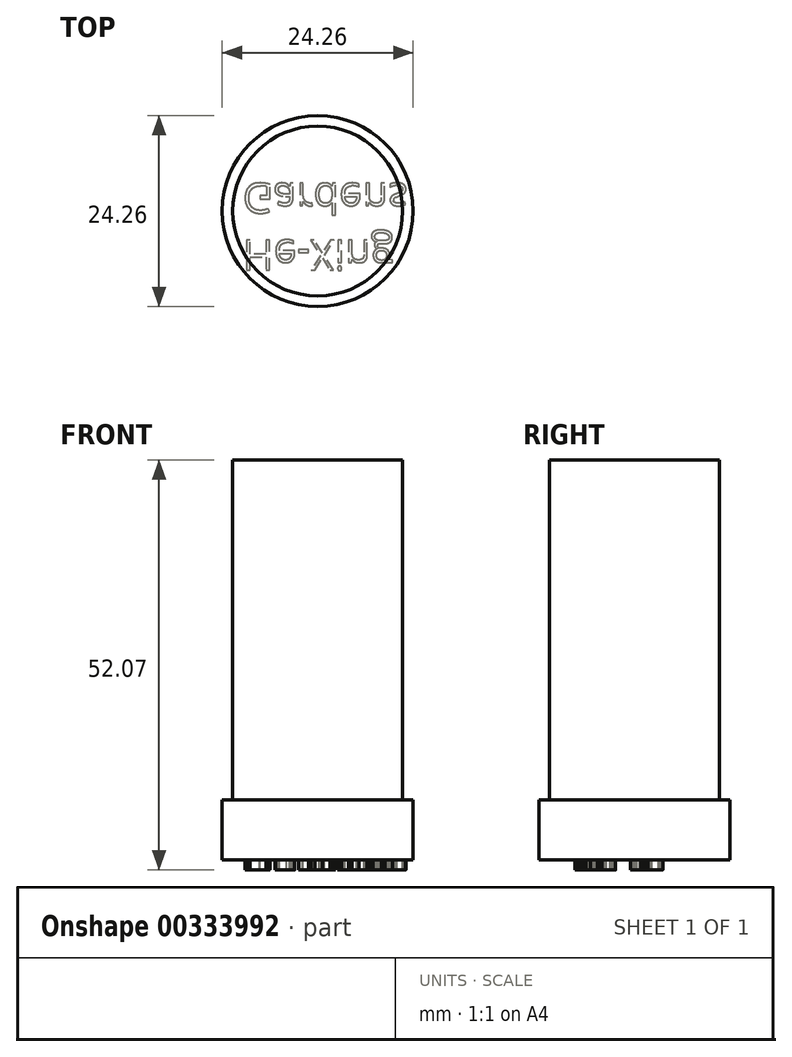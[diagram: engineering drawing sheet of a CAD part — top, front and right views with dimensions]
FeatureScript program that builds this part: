
annotation { "Feature Type Name" : "Feature", "Feature Type Description" : "" }
export const myFeature = defineFeature(function(context is Context, id is Id, definition is map)
    precondition{}
    {
        {
            var Q0;
            Q0=qCreatedBy(makeId("Top.planeOp"),FACE);
            var sketch = newSketch(context, id + "F0", { "sketchPlane" : qUnion([Q0])});
            skCircle(sketch, "E0", {"center": v(0, 0) * mm, "radius": 12.13 * mm});
            skCircle(sketch, "E1", {"center": v(0, 0) * mm, "radius": 10.8 * mm});
            skSolve(sketch);
        }
        {
            var Q0;
            Q0=makeQuery(id+"F0.imprint","IMPRINT",FACE,{"disambiguationData":[TD([[makeQuery(id+"F0.imprint","IMPRINT",EDGE,{"derivedFrom":sQuery(id+"F0.wireOp",EDGE,"E1")}),1.0]])]});
            extrude(context, id + "F1", {"entities" : qUnion([Q0]), "depth" : 50.8 * mm});
        }
        {
            var Q0;
            Q0 = qSketchRegion(id + "F0", true);
            extrude(context, id + "F2", {"entities" : qUnion([Q0]), "operationType" : NewBodyOperationType.ADD, "depth" : 7.62 * mm});
        }
        {
            var Q0;
            {var subQ0=sQuery(id+"F0.wireOp",EDGE,"E1");Q0=makeQuery(id+"F2.boolean.opBoolean","MERGE",FACE,{"derivedFrom":[makeQuery(id+"F1.opExtrude","CAP_FACE",FACE,{"disambiguationData":[OSD([subQ0])],"isStart":true}),makeQuery(id+"F2.opExtrude","CAP_FACE",FACE,{"disambiguationData":[OSD([sQuery(id+"F0.wireOp",EDGE,"E0"),subQ0])],"isStart":true})]});}
            var sketch = newSketch(context, id + "F3", { "sketchPlane" : qUnion([Q0])});
            skText(sketch, "E2", { "text": "He-Xing\nGardens", "fontName": "OpenSans-Regular.ttf"});
            const initialGuessF3  = {"E2": [-0.00953, 0.00368, 1, 0, 0.00382]};
            skSetInitialGuess(sketch, initialGuessF3);
            skSolve(sketch);
        }
        {
            var Q0;
            Q0 = qSketchRegion(id + "F3", true);
            extrude(context, id + "F4", {"entities" : qUnion([Q0]), "operationType" : NewBodyOperationType.ADD, "depth" : 1.27 * mm});
        }
    });
